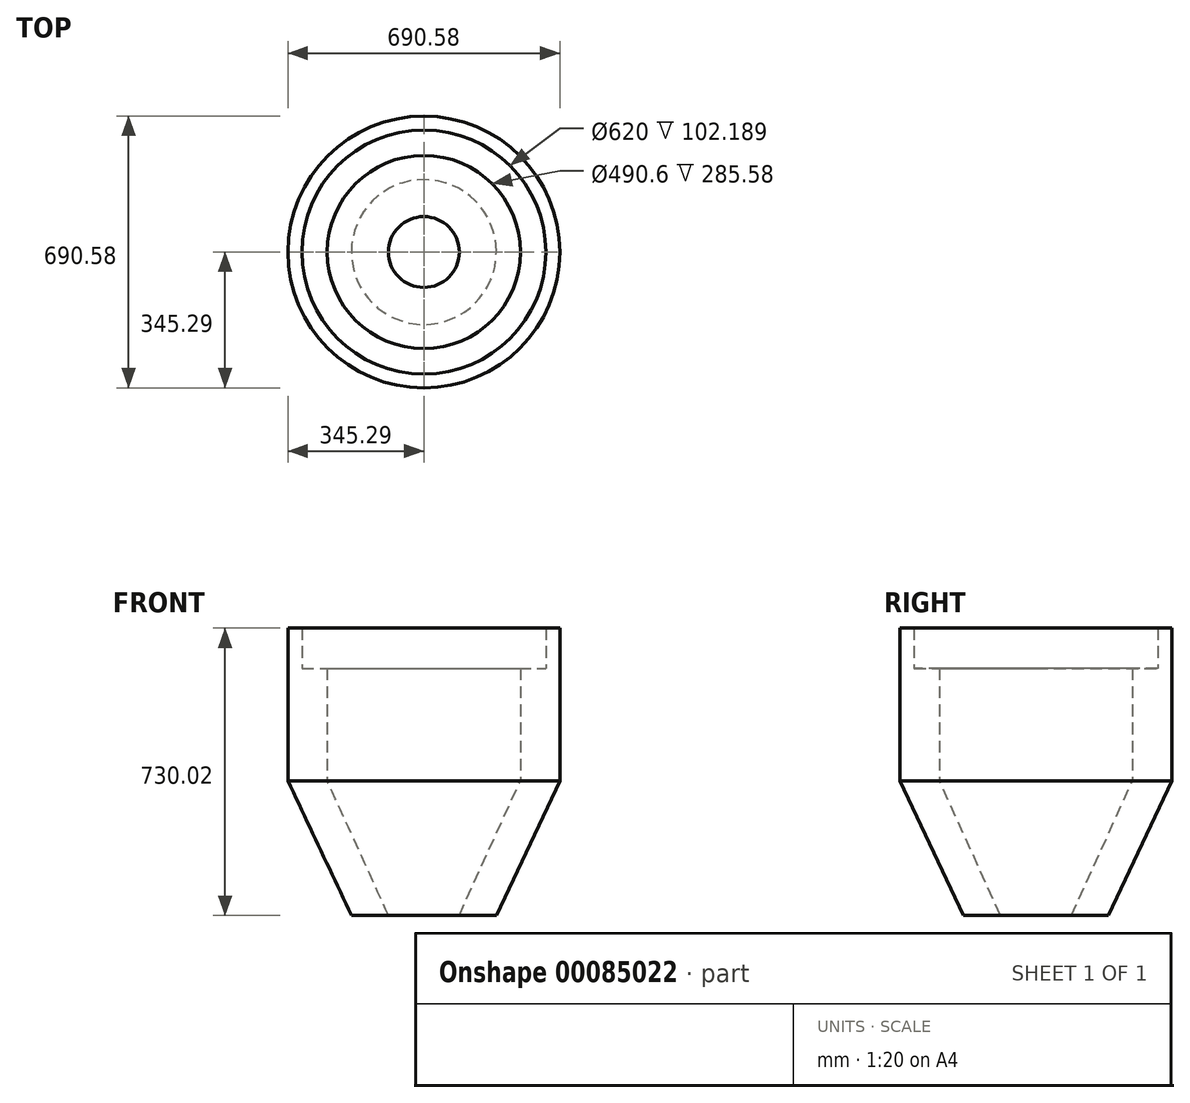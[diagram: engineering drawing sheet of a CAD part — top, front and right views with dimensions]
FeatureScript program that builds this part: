
annotation { "Feature Type Name" : "Feature", "Feature Type Description" : "" }
export const myFeature = defineFeature(function(context is Context, id is Id, definition is map)
    precondition{}
    {
        {
            var Q0;
            Q0=qCreatedBy(makeId("Front.planeOp"),FACE);
            var sketch = newSketch(context, id + "F0", { "sketchPlane" : qUnion([Q0])});
            skLineSegment(sketch, "E0", {"start": v(0, 285.58) * mm, "end": v(0, 387.77) * mm});
            skLineSegment(sketch, "E1", {"start": v(310, 387.77) * mm, "end": v(345.29, 387.77) * mm});
            skLineSegment(sketch, "E2", {"start": v(345.29, 387.77) * mm, "end": v(345.29, 0) * mm});
            skLineSegment(sketch, "E3", {"start": v(345.29, 0) * mm, "end": v(184.1, -342.25) * mm});
            skLineSegment(sketch, "E4", {"start": v(184.1, -342.25) * mm, "end": v(90, -342.25) * mm});
            skLineSegment(sketch, "E5", {"start": v(90, -342.25) * mm, "end": v(245.3, 0) * mm});
            skLineSegment(sketch, "E6", {"start": v(245.3, 0) * mm, "end": v(245.3, 285.58) * mm});
            skLineSegment(sketch, "E7", {"start": v(310, 285.58) * mm, "end": v(310, 387.77) * mm});
            skLineSegment(sketch, "E8", {"start": v(310, 285.58) * mm, "end": v(0, 285.58) * mm});
            skLineSegment(sketch, "E9", {"start": v(0, -342.66) * mm, "end": v(90, -342.25) * mm});
            skSolve(sketch);
        }
        {
            var Q0;
            Q0 = qSketchRegion(id + "F0", true);
            var Q1;
            Q1=sQuery(id+"F0.wireOp",EDGE,"E0");
            revolve(context, id + "F1", {"entities" : qUnion([Q0]), "axis" : qUnion([Q1]), "revolveType" : RevolveType.FULL});
        }
    });
